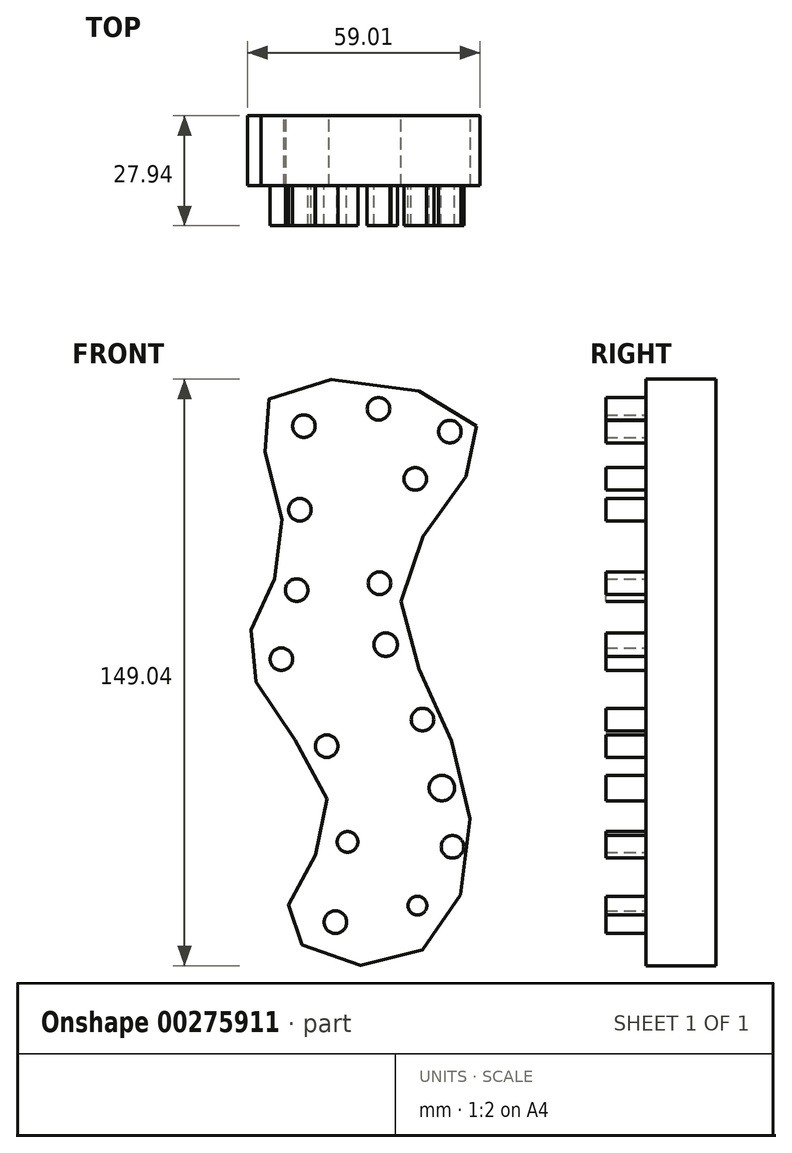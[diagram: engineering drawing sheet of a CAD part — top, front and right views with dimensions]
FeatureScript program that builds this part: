
annotation { "Feature Type Name" : "Feature", "Feature Type Description" : "" }
export const myFeature = defineFeature(function(context is Context, id is Id, definition is map)
    precondition{}
    {
        {
            var Q0;
            Q0=qCreatedBy(makeId("Front.planeOp"),FACE);
            var sketch = newSketch(context, id + "F0", { "sketchPlane" : qUnion([Q0])});
            skFitSpline(sketch, "E0", {"points": [v(18.34, 59.24) * mm, v(-33.5, 66.98) * mm, v(-30.6, 30.05) * mm, v(-39.63, 0) * mm, v(-19.18, -38.93) * mm, v(-29.85, -67.22) * mm, v(0, -76.37) * mm, v(15.6, -32.24) * mm, v(0, 21.45) * mm, v(18.34, 59.24) * mm]});
            skSolve(sketch);
        }
        {
            var Q0;
            Q0 = qSketchRegion(id + "F0", true);
            extrude(context, id + "F1", {"entities" : qUnion([Q0]), "depth" : 17.78 * mm});
        }
        {
            var Q0;
            Q0=makeQuery(id+"F1.opExtrude","CAP_FACE",FACE,{"disambiguationData":[OSD([sQuery(id+"F0.wireOp",EDGE,"E0")])],"isStart":false});
            var sketch = newSketch(context, id + "F2", { "sketchPlane" : qUnion([Q0])});
            skCircle(sketch, "E1", {"center": v(-25.5, 59.21) * mm, "radius": 2.87 * mm});
            skCircle(sketch, "E2", {"center": v(-6.54, 63.6) * mm, "radius": 2.87 * mm});
            skCircle(sketch, "E3", {"center": v(11.6, 57.81) * mm, "radius": 2.87 * mm});
            skCircle(sketch, "E4", {"center": v(-26.52, 37.95) * mm, "radius": 2.87 * mm});
            skCircle(sketch, "E5", {"center": v(2.78, 45.8) * mm, "radius": 2.87 * mm});
            skCircle(sketch, "E6", {"center": v(-6.3, 19.3) * mm, "radius": 2.87 * mm});
            skCircle(sketch, "E7", {"center": v(-27.34, 17.54) * mm, "radius": 2.87 * mm});
            skCircle(sketch, "E8", {"center": v(-31.22, 0) * mm, "radius": 2.87 * mm});
            skCircle(sketch, "E9", {"center": v(-19.71, -22.1) * mm, "radius": 2.87 * mm});
            skCircle(sketch, "E10", {"center": v(9.56, -32.74) * mm, "radius": 3.25 * mm});
            skCircle(sketch, "E11", {"center": v(4.63, -15.36) * mm, "radius": 2.87 * mm});
            skCircle(sketch, "E12", {"center": v(12.25, -47.69) * mm, "radius": 2.87 * mm});
            skCircle(sketch, "E13", {"center": v(-14.42, -46.42) * mm, "radius": 2.64 * mm});
            skCircle(sketch, "E14", {"center": v(3.35, -62.6) * mm, "radius": 2.39 * mm});
            skCircle(sketch, "E15", {"center": v(-17.5, -66.83) * mm, "radius": 2.87 * mm});
            skCircle(sketch, "E16", {"center": v(-4.7, 3.68) * mm, "radius": 2.98 * mm});
            skSolve(sketch);
        }
        {
            var Q0;
            Q0 = qSketchRegion(id + "F2", true);
            extrude(context, id + "F3", {"entities" : qUnion([Q0]), "operationType" : NewBodyOperationType.ADD, "depth" : 10.16 * mm});
        }
    });
